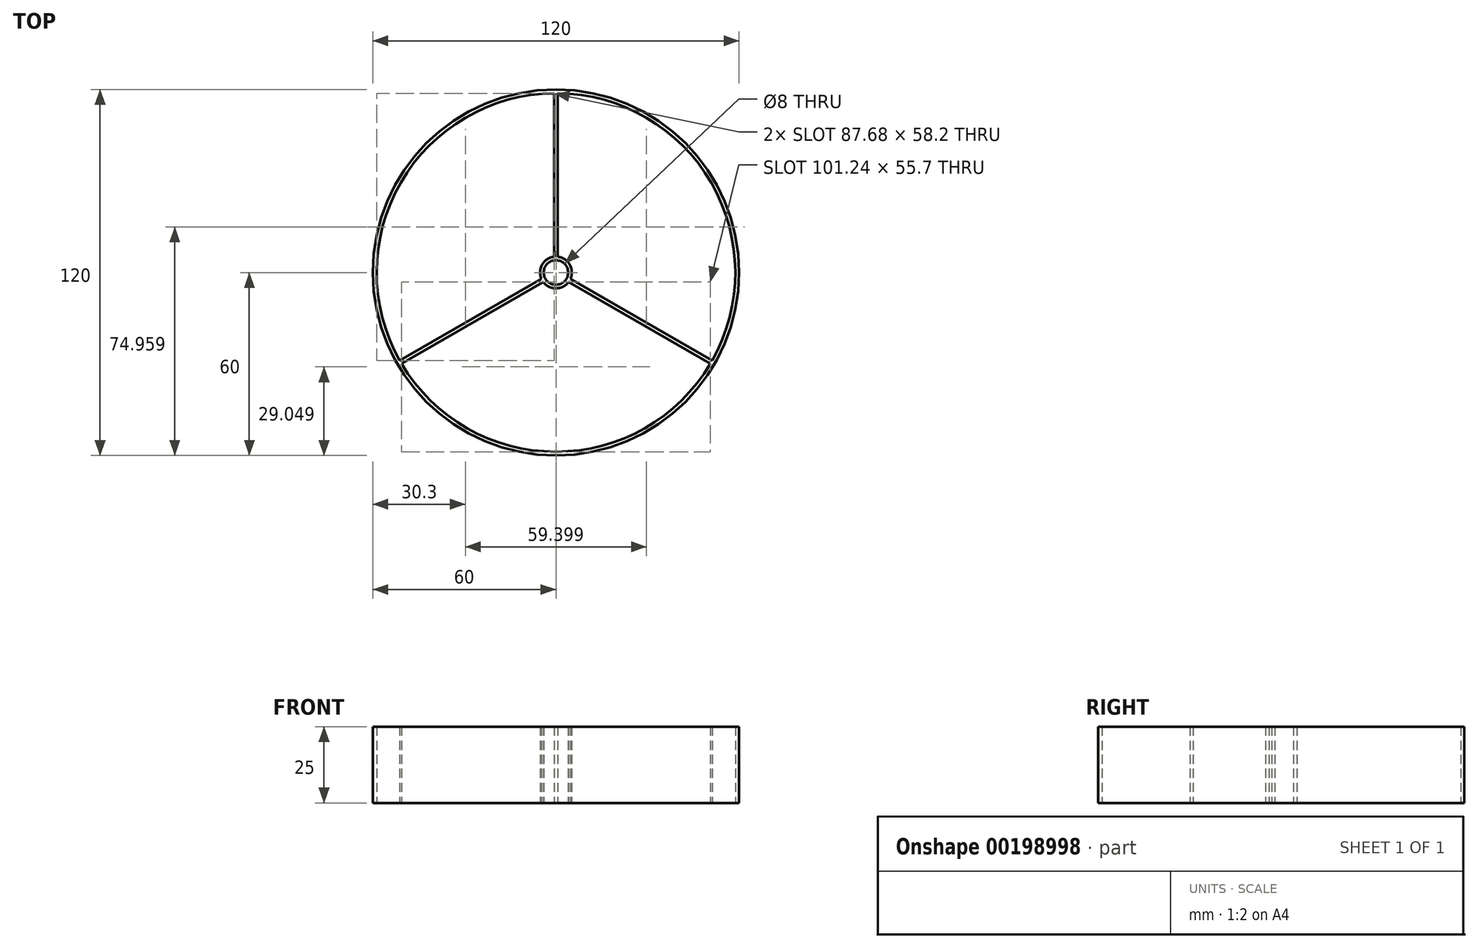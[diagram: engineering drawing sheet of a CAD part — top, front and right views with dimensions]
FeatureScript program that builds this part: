
annotation { "Feature Type Name" : "Feature", "Feature Type Description" : "" }
export const myFeature = defineFeature(function(context is Context, id is Id, definition is map)
    precondition{}
    {
        {
            var Q0;
            Q0=qCreatedBy(makeId("Top.planeOp"),FACE);
            var sketch = newSketch(context, id + "F0", { "sketchPlane" : qUnion([Q0])});
            skCircle(sketch, "E0", {"center": v(0, 0) * mm, "radius": 60 * mm});
            skArc(sketch, "E1.0", {"start": v(-0.6, 58.8) * mm, "mid": v(-50.92, 29.4) * mm, "end": v(-51.22, -28.88) * mm});
            skCircle(sketch, "E2", {"center": v(0, 0) * mm, "radius": 4 * mm});
            skArc(sketch, "E3", {"start": v(-0.6, 5.17) * mm, "mid": v(-4.5, 2.6) * mm, "end": v(-4.77, -2.06) * mm});
            skLineSegment(sketch, "E4.left", {"start": v(-0.6, 58.8) * mm, "end": v(-0.6, 5.17) * mm});
            skLineSegment(sketch, "E4.right", {"start": v(0.6, 58.8) * mm, "end": v(0.6, 5.17) * mm});
            skLineSegment(sketch, "E5.1.0", {"start": v(-50.62, -29.92) * mm, "end": v(-4.17, -3.1) * mm});
            skLineSegment(sketch, "E5.1.1", {"start": v(-51.22, -28.88) * mm, "end": v(-4.77, -2.06) * mm});
            skLineSegment(sketch, "E5.2.0", {"start": v(51.22, -28.88) * mm, "end": v(4.77, -2.06) * mm});
            skLineSegment(sketch, "E5.2.1", {"start": v(50.62, -29.92) * mm, "end": v(4.17, -3.1) * mm});
            skArc(sketch, "E6.trimOffspring", {"start": v(4.77, -2.06) * mm, "mid": v(4.5, 2.6) * mm, "end": v(0.6, 5.17) * mm});
            skArc(sketch, "E7.trimOffspring", {"start": v(-4.17, -3.1) * mm, "mid": v(0, -5.2) * mm, "end": v(4.17, -3.1) * mm});
            skArc(sketch, "E8.trimOffspring", {"start": v(-50.62, -29.92) * mm, "mid": v(0, -58.8) * mm, "end": v(50.62, -29.92) * mm});
            skArc(sketch, "E9.trimOffspring", {"start": v(51.22, -28.88) * mm, "mid": v(50.92, 29.4) * mm, "end": v(0.6, 58.8) * mm});
            skSolve(sketch);
        }
        {
            var Q0;
            Q0 = qSketchRegion(id + "F0", true);
            extrude(context, id + "F1", {"entities" : qUnion([Q0]), "depth" : 25 * mm});
        }
    });
